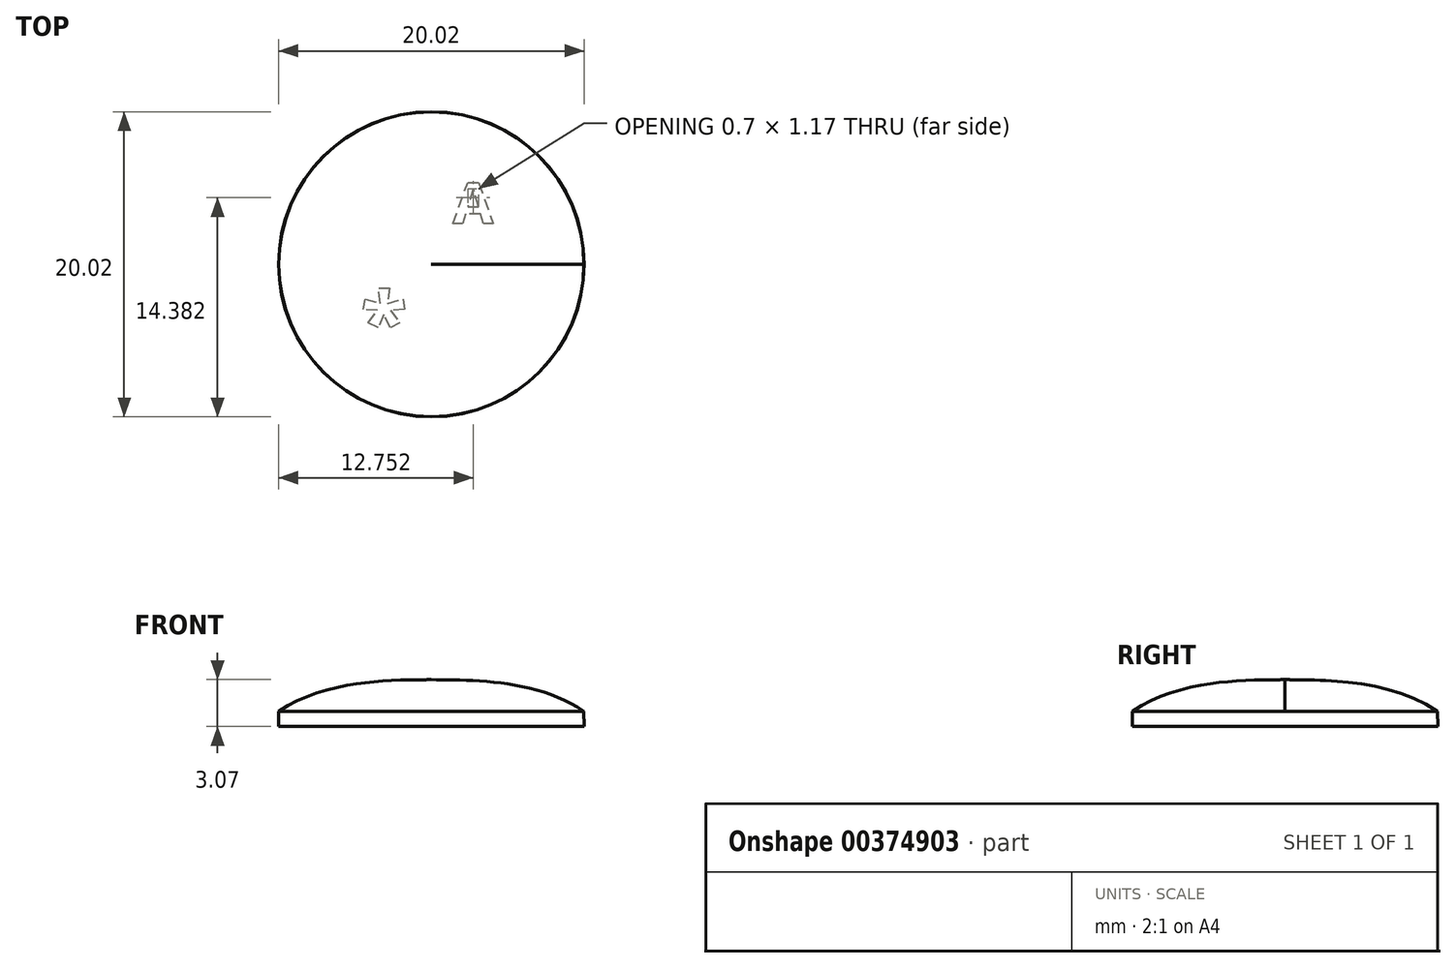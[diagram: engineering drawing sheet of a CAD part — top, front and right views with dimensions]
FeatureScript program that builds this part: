
annotation { "Feature Type Name" : "Feature", "Feature Type Description" : "" }
export const myFeature = defineFeature(function(context is Context, id is Id, definition is map)
    precondition{}
    {
        {
            var Q0;
            Q0=qCreatedBy(makeId("Front.planeOp"),FACE);
            var sketch = newSketch(context, id + "F0", { "sketchPlane" : qUnion([Q0])});
            skLineSegment(sketch, "E0", {"start": v(0, 0) * mm, "end": v(10.01, 0) * mm});
            skLineSegment(sketch, "E1", {"start": v(10.01, 0) * mm, "end": v(10, 1) * mm});
            skLineSegment(sketch, "E2", {"start": v(0, 0) * mm, "end": v(0, 3.07) * mm});
            skFitSpline(sketch, "E3", {"points": [v(10, 1) * mm, v(0, 3.07) * mm], "startDerivative": vector(-9.28, 6.34) * mm, "endDerivative": vector(-7.55, 0.06) * mm});
            skSolve(sketch);
        }
        {
            var Q0;
            Q0 = qSketchRegion(id + "F0", true);
            var Q1;
            Q1=sQuery(id+"F0.wireOp",EDGE,"E2");
            revolve(context, id + "F1", {"entities" : qUnion([Q0]), "axis" : qUnion([Q1]), "revolveType" : RevolveType.FULL});
        }
        {
            var Q0;
            Q0=qCreatedBy(makeId("Top.planeOp"),FACE);
            cPlane(context, id + "F2", {"entities" : qUnion([Q0]), "cplaneType" : CPlaneType.OFFSET, "offset" : 1 * mm, "width" : 150 * mm, "height" : 150 * mm});
        }
        {
            var Q0;
            Q0=qCreatedBy(id+"F2.planeOp",FACE);
            var sketch = newSketch(context, id + "F3", { "sketchPlane" : qUnion([Q0])});
            skText(sketch, "E4", { "text": "A", "fontName": "OpenSans-Bold.ttf"});
            skText(sketch, "E5", { "text": "*", "fontName": "OpenSans-Bold.ttf"});
            const initialGuessF3  = {"E4": [0.00143, 0.00266, 1, 0, 0.00273], "E5": [-0.00462, -0.0058, 1, 0, 0.00402]};
            skSetInitialGuess(sketch, initialGuessF3);
            skSolve(sketch);
        }
        {
            var Q0;
            Q0 = qSketchRegion(id + "F3", true);
            extrude(context, id + "F4", {"entities" : qUnion([Q0]), "operationType" : NewBodyOperationType.REMOVE, "oppositeDirection" : true, "depth" : 0.05 * mm});
        }
    });
